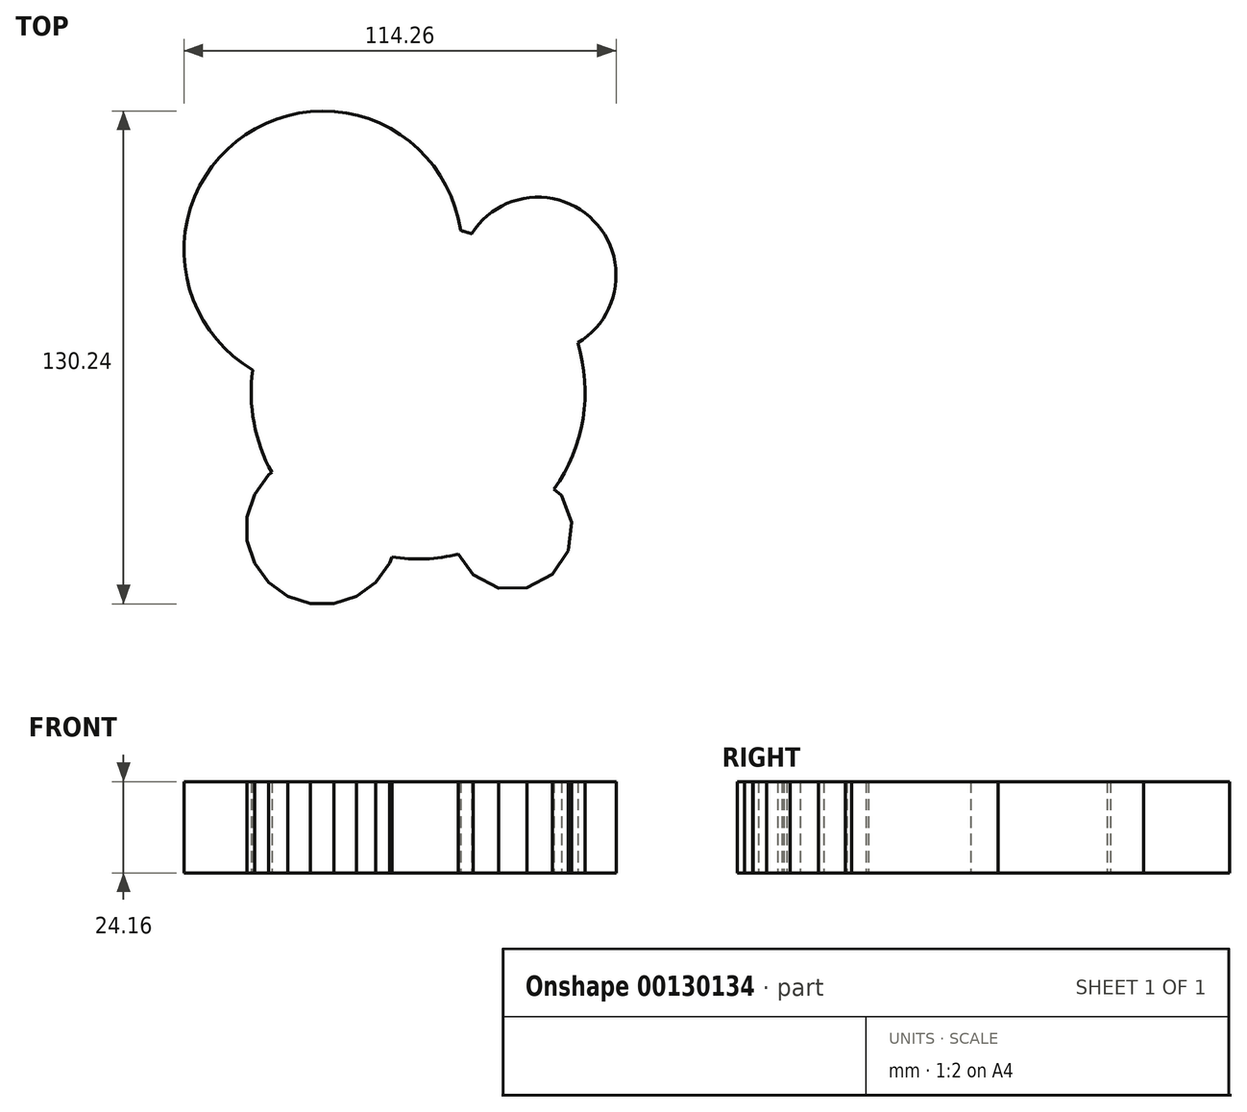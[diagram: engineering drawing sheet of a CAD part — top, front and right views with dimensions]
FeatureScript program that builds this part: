
annotation { "Feature Type Name" : "Feature", "Feature Type Description" : "" }
export const myFeature = defineFeature(function(context is Context, id is Id, definition is map)
    precondition{}
    {
        {
            var Q0;
            Q0=qCreatedBy(makeId("Top.planeOp"),FACE);
            var sketch = newSketch(context, id + "F0", { "sketchPlane" : qUnion([Q0])});
            skArc(sketch, "E0", {"start": v(-37.86, 22.73) * mm, "mid": v(-44.15, 0.77) * mm, "end": v(-38.63, -21.4) * mm});
            skArc(sketch, "E1", {"start": v(-6.67, 43.65) * mm, "mid": v(-36.03, 53.7) * mm, "end": v(-37.86, 22.73) * mm});
            skArc(sketch, "E2", {"start": v(42.2, 13) * mm, "mid": v(46.48, 45.24) * mm, "end": v(14.13, 41.84) * mm});
            skArc(sketch, "E3", {"start": v(43.72, 6.18) * mm, "mid": v(50.45, 53.03) * mm, "end": v(3.99, 43.98) * mm});
            skArc(sketch, "E4.cCircle", {"start": v(10.95, -42.78) * mm, "mid": v(33.6, -49.12) * mm, "end": v(35.9, -25.71) * mm, "construction": true});
            skLineSegment(sketch, "E4.0", {"start": v(40.61, -34.46) * mm, "end": v(39.74, -41.97) * mm});
            skLineSegment(sketch, "E4.1", {"start": v(39.74, -41.97) * mm, "end": v(35.48, -48.22) * mm});
            skLineSegment(sketch, "E4.2", {"start": v(35.48, -48.22) * mm, "end": v(28.8, -51.78) * mm});
            skLineSegment(sketch, "E4.3", {"start": v(28.8, -51.78) * mm, "end": v(21.23, -51.82) * mm});
            skLineSegment(sketch, "E4.4", {"start": v(21.23, -51.82) * mm, "end": v(14.51, -48.34) * mm});
            skLineSegment(sketch, "E4.5", {"start": v(14.51, -48.34) * mm, "end": v(10.18, -42.13) * mm});
            skLineSegment(sketch, "E4.11", {"start": v(35.93, -25.67) * mm, "end": v(37.9, -27.4) * mm});
            skLineSegment(sketch, "E4.12", {"start": v(37.9, -27.4) * mm, "end": v(40.61, -34.46) * mm});
            skPoint(sketch, "E4.0.midPoint", {"position": v(40.18, -38.22) * mm});
            skArc(sketch, "E5.cCircle", {"start": v(-38.63, -21.4) * mm, "mid": v(-30.51, -55.3) * mm, "end": v(-6.5, -30.01) * mm, "construction": true});
            skLineSegment(sketch, "E5.0", {"start": v(-22.23, -55.98) * mm, "end": v(-28.51, -55.98) * mm});
            skLineSegment(sketch, "E5.1", {"start": v(-28.51, -55.98) * mm, "end": v(-34.49, -54.03) * mm});
            skLineSegment(sketch, "E5.2", {"start": v(-34.49, -54.03) * mm, "end": v(-39.57, -50.34) * mm});
            skLineSegment(sketch, "E5.3", {"start": v(-39.57, -50.34) * mm, "end": v(-43.26, -45.26) * mm});
            skLineSegment(sketch, "E5.4", {"start": v(-43.26, -45.26) * mm, "end": v(-45.2, -39.28) * mm});
            skLineSegment(sketch, "E5.5", {"start": v(-45.2, -39.28) * mm, "end": v(-45.2, -33) * mm});
            skLineSegment(sketch, "E5.6", {"start": v(-45.2, -33) * mm, "end": v(-43.26, -27.02) * mm});
            skLineSegment(sketch, "E5.7", {"start": v(-43.26, -27.02) * mm, "end": v(-39.57, -21.94) * mm});
            skLineSegment(sketch, "E5.8", {"start": v(-39.57, -21.94) * mm, "end": v(-34.49, -18.25) * mm});
            skLineSegment(sketch, "E5.14", {"start": v(-6.5, -30.01) * mm, "end": v(-5.54, -33) * mm});
            skLineSegment(sketch, "E5.15", {"start": v(-5.54, -33) * mm, "end": v(-5.54, -39.28) * mm});
            skLineSegment(sketch, "E5.16", {"start": v(-5.54, -39.28) * mm, "end": v(-7.48, -45.26) * mm});
            skLineSegment(sketch, "E5.17", {"start": v(-7.48, -45.26) * mm, "end": v(-11.17, -50.34) * mm});
            skLineSegment(sketch, "E5.18", {"start": v(-11.17, -50.34) * mm, "end": v(-16.25, -54.03) * mm});
            skLineSegment(sketch, "E5.19", {"start": v(-16.25, -54.03) * mm, "end": v(-22.23, -55.98) * mm});
            skPoint(sketch, "E5.0.midPoint", {"position": v(-25.37, -55.98) * mm});
            skArc(sketch, "E6.trimOffspring", {"start": v(11.2, 42.71) * mm, "mid": v(-45.64, 68.03) * mm, "end": v(-43.77, 5.84) * mm});
            skArc(sketch, "E7.trimOffspring", {"start": v(14.13, 41.84) * mm, "mid": v(3.84, 44) * mm, "end": v(-6.67, 43.65) * mm});
            skArc(sketch, "E8.trimOffspring", {"start": v(31.65, 30.8) * mm, "mid": v(31.05, 31.4) * mm, "end": v(30.44, 32) * mm});
            skPoint(sketch, "E9.orphan", {"position": v(32.2, -22.4) * mm});
            skArc(sketch, "E10.trimOffspring", {"start": v(35.9, -25.71) * mm, "mid": v(43.58, -7.1) * mm, "end": v(42.2, 13) * mm});
            skArc(sketch, "E11.trimOffspring", {"start": v(-7, -43.6) * mm, "mid": v(2.02, -44.11) * mm, "end": v(10.95, -42.78) * mm});
            skPoint(sketch, "E12.orphan", {"position": v(-22.23, -16.3) * mm});
            skPoint(sketch, "E13.orphan", {"position": v(-7.48, -27.02) * mm});
            skSolve(sketch);
        }
        {
            var Q0;
            {var subQ0=sQuery(id+"F0.wireOp",EDGE,"E7.trimOffspring");var subQ1=sQuery(id+"F0.wireOp",EDGE,"E3");var subQ2=makeQuery(id+"F0.imprint","INTERSECT",VERTEX,{"derivedFrom":[subQ1,subQ0]});Q0=makeQuery(id+"F0.imprint","IMPRINT",FACE,{"disambiguationData":[TD([[makeQuery(id+"F0.imprint","IMPRINT",EDGE,{"disambiguationData":[TD([[subQ2,1.0]])],"derivedFrom":subQ1}),1.0]])]});}
            var Q1;
            {var subQ5=sQuery(id+"F0.wireOp",EDGE,"E1");Q1=makeQuery(id+"F0.imprint","IMPRINT",FACE,{"disambiguationData":[TD([[makeQuery(id+"F0.imprint","IMPRINT",EDGE,{"derivedFrom":subQ5}),1.0]])]});}
            var Q2;
            {var subQ7=sQuery(id+"F0.wireOp",EDGE,"E1");Q2=makeQuery(id+"F0.imprint","IMPRINT",FACE,{"disambiguationData":[TD([[makeQuery(id+"F0.imprint","IMPRINT",EDGE,{"derivedFrom":subQ7}),-1.0]])]});}
            extrude(context, id + "F1", {"entities" : qUnion([Q0, Q1, Q2]), "depth" : 24.16 * mm});
        }
    });
